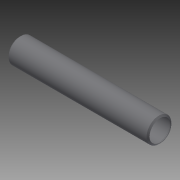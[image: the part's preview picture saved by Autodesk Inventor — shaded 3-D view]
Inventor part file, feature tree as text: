
AUTODESK INVENTOR PART (.ipt)
format: ipt  version: 2014 (Build 180170000, 170)  size: 119,808 bytes
history: native  units: in
note: dims shown in document units (in); Inventor stores cm internally (conversion verified against a paired STEP export)
features: other x56, revolve x1, sketch x1
ambient origin geometry x8: Origin, YZ Plane, XZ Plane, XY Plane, X Axis, Y Axis, Z Axis, Center Point
bodies: Solid1 (feature_tree)
feature tree (58):
  revolve  "Revolution1"  [1 undecoded]
  other  "o1_XY"
  other  "o1_YZ"
  other  "o1_ZX"
  other  "o1_X"
  other  "o1_Y"
  other  "o1_Z"
  other  "o1_Center"
  other  "o2_XY"
  other  "o2_YZ"
  other  "o2_ZX"
  other  "o2_X"
  other  "o2_Y"
  other  "o2_Z"
  other  "o2_Center"
  other  "t1_XY"
  other  "t1_YZ"
  other  "t1_ZX"
  other  "t1_X"
  other  "t1_Y"
  other  "t1_Z"
  other  "t1_Center"
  other  "t2_XY"
  other  "t2_YZ"
  other  "t2_ZX"
  other  "t2_X"
  other  "t2_Y"
  other  "t2_Z"
  other  "t2_Center"
  other  "t3_XY"
  other  "t3_YZ"
  other  "t3_ZX"
  other  "t3_X"
  other  "t3_Y"
  other  "t3_Z"
  other  "t3_Center"
  other  "t4_XY"
  other  "t4_YZ"
  other  "t4_ZX"
  other  "t4_X"
  other  "t4_Y"
  other  "t4_Z"
  other  "t4_Center"
  other  "tube1_XY"
  other  "tube1_YZ"
  other  "tube1_ZX"
  other  "tube1_X"
  other  "tube1_Y"
  other  "tube1_Z"
  other  "tube1_Center"
  other  "tube2_XY"
  other  "tube2_YZ"
  other  "tube2_ZX"
  other  "tube2_X"
  other  "tube2_Y"
  other  "tube2_Z"
  other  "tube2_Center"
  sketch  "Sketch_5"  dims[d0=360.0deg]
note: 1 required parameter value undecoded (feature->parameter linkage not recoverable at this tier; creation-order binding heuristic only, values carry confidence <= 0.55)
